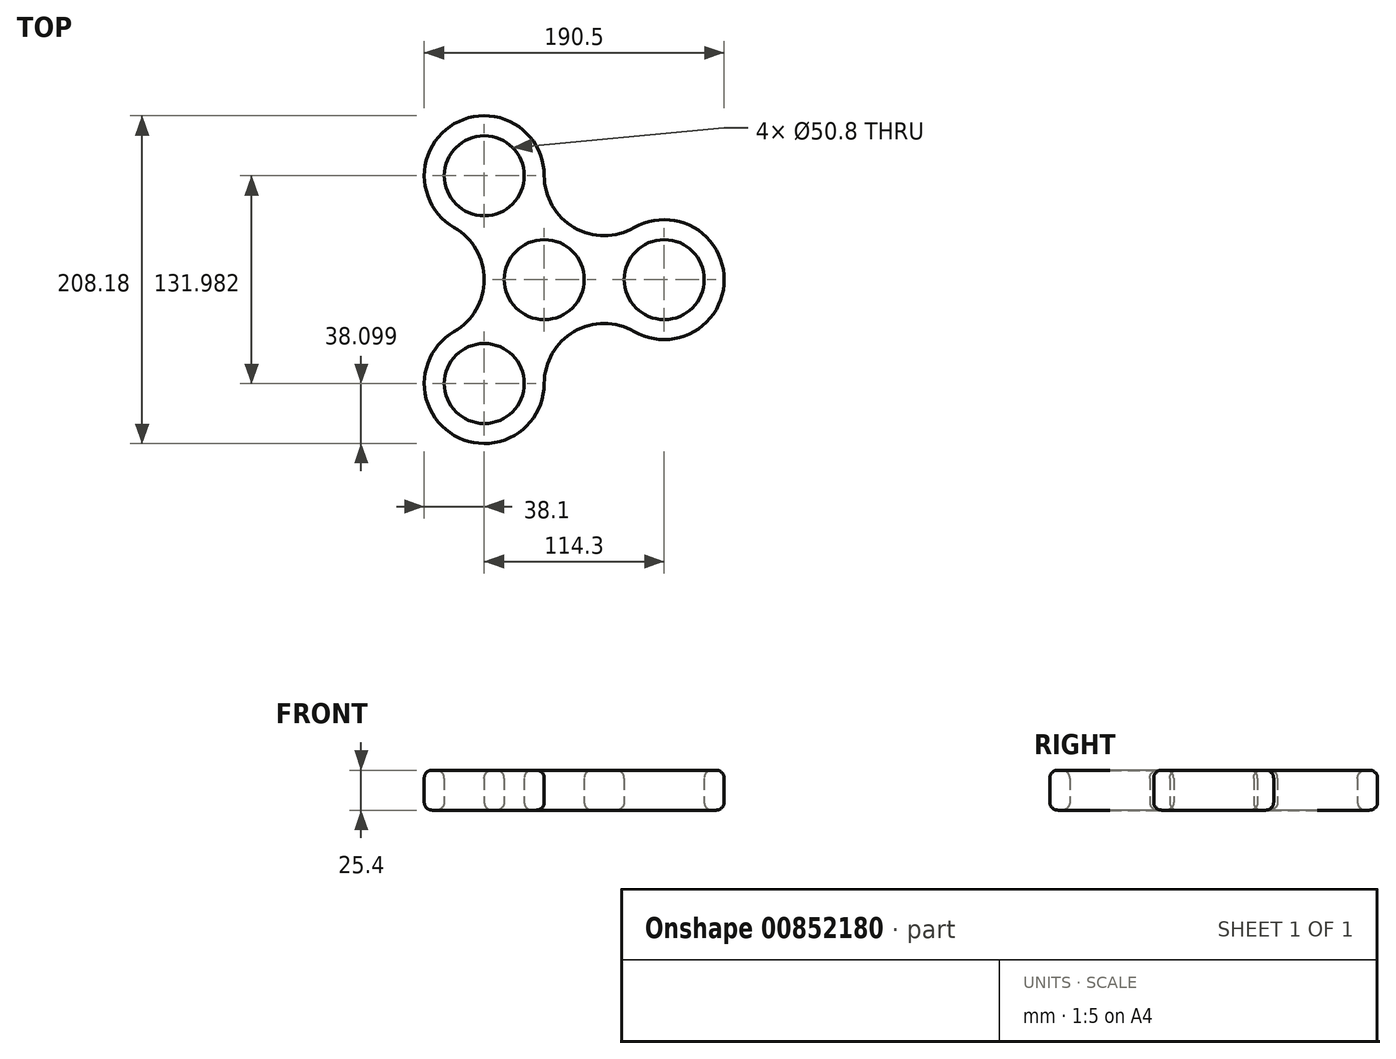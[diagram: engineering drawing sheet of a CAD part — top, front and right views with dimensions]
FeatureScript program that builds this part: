
annotation { "Feature Type Name" : "Feature", "Feature Type Description" : "" }
export const myFeature = defineFeature(function(context is Context, id is Id, definition is map)
    precondition{}
    {
        {
            var Q0;
            Q0=qCreatedBy(makeId("Top.planeOp"),FACE);
            var sketch = newSketch(context, id + "F0", { "sketchPlane" : qUnion([Q0])});
            skCircle(sketch, "E0.cCircle", {"center": v(0, 0) * mm, "radius": 76.2 * mm});
            skLineSegment(sketch, "E0.0", {"start": v(38.1, 66) * mm, "end": v(76.2, 0) * mm});
            skLineSegment(sketch, "E0.1", {"start": v(76.2, 0) * mm, "end": v(38.1, -66) * mm});
            skLineSegment(sketch, "E0.2", {"start": v(38.1, -66) * mm, "end": v(-38.1, -66) * mm});
            skLineSegment(sketch, "E0.3", {"start": v(-38.1, -66) * mm, "end": v(-76.2, 0) * mm});
            skLineSegment(sketch, "E0.4", {"start": v(-76.2, 0) * mm, "end": v(-38.1, 66) * mm});
            skLineSegment(sketch, "E0.5", {"start": v(38.1, 66) * mm, "end": v(76.2, 66) * mm});
            skCircle(sketch, "E1", {"center": v(0, 0) * mm, "radius": 25.4 * mm});
            skCircle(sketch, "E2", {"center": v(-38.1, 66) * mm, "radius": 25.4 * mm});
            skCircle(sketch, "E3", {"center": v(38.1, 66) * mm, "radius": 25.4 * mm});
            skCircle(sketch, "E4", {"center": v(76.2, 0) * mm, "radius": 25.4 * mm});
            skCircle(sketch, "E5", {"center": v(38.1, -66) * mm, "radius": 25.4 * mm});
            skCircle(sketch, "E6", {"center": v(-38.1, -66) * mm, "radius": 25.4 * mm});
            skCircle(sketch, "E7", {"center": v(-76.2, 0) * mm, "radius": 25.4 * mm});
            skCircle(sketch, "E8.0", {"center": v(-38.1, 66) * mm, "radius": 38.1 * mm});
            skCircle(sketch, "E9.0", {"center": v(38.1, 66) * mm, "radius": 38.1 * mm});
            skCircle(sketch, "E10.0", {"center": v(76.2, 0) * mm, "radius": 38.1 * mm});
            skCircle(sketch, "E11.0", {"center": v(-76.2, 0) * mm, "radius": 38.1 * mm});
            skCircle(sketch, "E12.0", {"center": v(-38.1, -66) * mm, "radius": 38.1 * mm});
            skCircle(sketch, "E13.0", {"center": v(38.1, -66) * mm, "radius": 38.1 * mm});
            skSolve(sketch);
        }
        {
            var Q0;
            {var subQ0=sQuery(id+"F0.wireOp",EDGE,"E10.0");var subQ1=sQuery(id+"F0.wireOp",EDGE,"E0.cCircle");var subQ2=makeQuery(id+"F0.imprint","INTERSECT",VERTEX,{"disambiguationData":[OD(0.0)],"derivedFrom":[subQ1,subQ0]});Q0=makeQuery(id+"F0.imprint","IMPRINT",FACE,{"disambiguationData":[TD([[makeQuery(id+"F0.imprint","IMPRINT",EDGE,{"disambiguationData":[TD([[subQ2,1.0]])],"derivedFrom":subQ1}),-1.0]])]});}
            var Q1;
            {var subQ0=sQuery(id+"F0.wireOp",EDGE,"E10.0");var subQ1=sQuery(id+"F0.wireOp",EDGE,"E0.cCircle");var subQ2=makeQuery(id+"F0.imprint","INTERSECT",VERTEX,{"disambiguationData":[OD(0.0)],"derivedFrom":[subQ1,subQ0]});Q1=makeQuery(id+"F0.imprint","IMPRINT",FACE,{"disambiguationData":[TD([[makeQuery(id+"F0.imprint","IMPRINT",EDGE,{"disambiguationData":[TD([[subQ2,1.0]])],"derivedFrom":subQ1}),1.0]])]});}
            var Q2;
            {var subQ0=sQuery(id+"F0.wireOp",EDGE,"E4");var subQ1=sQuery(id+"F0.wireOp",EDGE,"E0.0");var subQ2=makeQuery(id+"F0.imprint","INTERSECT",VERTEX,{"derivedFrom":[subQ1,subQ0]});Q2=makeQuery(id+"F0.imprint","IMPRINT",FACE,{"disambiguationData":[TD([[makeQuery(id+"F0.imprint","IMPRINT",EDGE,{"disambiguationData":[TD([[subQ2,-1.0]])],"derivedFrom":subQ0}),-1.0]])]});}
            var Q3;
            {var subQ0=sQuery(id+"F0.wireOp",EDGE,"E10.0");var subQ1=sQuery(id+"F0.wireOp",EDGE,"E0.cCircle");var subQ2=makeQuery(id+"F0.imprint","INTERSECT",VERTEX,{"disambiguationData":[OD(1.0)],"derivedFrom":[subQ1,subQ0]});Q3=makeQuery(id+"F0.imprint","IMPRINT",FACE,{"disambiguationData":[TD([[makeQuery(id+"F0.imprint","IMPRINT",EDGE,{"disambiguationData":[TD([[subQ2,-1.0]])],"derivedFrom":subQ1}),1.0]])]});}
            var Q4;
            Q4=makeQuery(id+"F0.imprint","IMPRINT",FACE,{"disambiguationData":[TD([[makeQuery(id+"F0.imprint","IMPRINT",EDGE,{"derivedFrom":sQuery(id+"F0.wireOp",EDGE,"E1")}),-1.0]])]});
            var Q5;
            {var subQ0=sQuery(id+"F0.wireOp",EDGE,"E12.0");var subQ1=sQuery(id+"F0.wireOp",EDGE,"E0.cCircle");var subQ2=makeQuery(id+"F0.imprint","INTERSECT",VERTEX,{"disambiguationData":[OD(1.0)],"derivedFrom":[subQ1,subQ0]});Q5=makeQuery(id+"F0.imprint","IMPRINT",FACE,{"disambiguationData":[TD([[makeQuery(id+"F0.imprint","IMPRINT",EDGE,{"disambiguationData":[TD([[subQ2,1.0]])],"derivedFrom":subQ1}),1.0]])]});}
            var Q6;
            {var subQ0=sQuery(id+"F0.wireOp",EDGE,"E6");var subQ1=sQuery(id+"F0.wireOp",EDGE,"E0.2");var subQ2=makeQuery(id+"F0.imprint","INTERSECT",VERTEX,{"derivedFrom":[subQ1,subQ0]});Q6=makeQuery(id+"F0.imprint","IMPRINT",FACE,{"disambiguationData":[TD([[makeQuery(id+"F0.imprint","IMPRINT",EDGE,{"disambiguationData":[TD([[subQ2,-1.0]])],"derivedFrom":subQ0}),-1.0]])]});}
            var Q7;
            {var subQ0=sQuery(id+"F0.wireOp",EDGE,"E12.0");var subQ1=sQuery(id+"F0.wireOp",EDGE,"E0.cCircle");var subQ2=makeQuery(id+"F0.imprint","INTERSECT",VERTEX,{"disambiguationData":[OD(0.0)],"derivedFrom":[subQ1,subQ0]});Q7=makeQuery(id+"F0.imprint","IMPRINT",FACE,{"disambiguationData":[TD([[makeQuery(id+"F0.imprint","IMPRINT",EDGE,{"disambiguationData":[TD([[subQ2,-1.0]])],"derivedFrom":subQ1}),-1.0]])]});}
            var Q8;
            {var subQ0=sQuery(id+"F0.wireOp",EDGE,"E12.0");var subQ1=sQuery(id+"F0.wireOp",EDGE,"E0.cCircle");var subQ2=makeQuery(id+"F0.imprint","INTERSECT",VERTEX,{"disambiguationData":[OD(0.0)],"derivedFrom":[subQ1,subQ0]});Q8=makeQuery(id+"F0.imprint","IMPRINT",FACE,{"disambiguationData":[TD([[makeQuery(id+"F0.imprint","IMPRINT",EDGE,{"disambiguationData":[TD([[subQ2,-1.0]])],"derivedFrom":subQ1}),1.0]])]});}
            var Q9;
            {var subQ0=sQuery(id+"F0.wireOp",EDGE,"E8.0");var subQ1=sQuery(id+"F0.wireOp",EDGE,"E0.cCircle");var subQ2=makeQuery(id+"F0.imprint","INTERSECT",VERTEX,{"disambiguationData":[OD(1.0)],"derivedFrom":[subQ1,subQ0]});Q9=makeQuery(id+"F0.imprint","IMPRINT",FACE,{"disambiguationData":[TD([[makeQuery(id+"F0.imprint","IMPRINT",EDGE,{"disambiguationData":[TD([[subQ2,1.0]])],"derivedFrom":subQ1}),1.0]])]});}
            var Q10;
            {var subQ0=sQuery(id+"F0.wireOp",EDGE,"E8.0");var subQ1=sQuery(id+"F0.wireOp",EDGE,"E0.cCircle");var subQ2=makeQuery(id+"F0.imprint","INTERSECT",VERTEX,{"disambiguationData":[OD(0.0)],"derivedFrom":[subQ1,subQ0]});Q10=makeQuery(id+"F0.imprint","IMPRINT",FACE,{"disambiguationData":[TD([[makeQuery(id+"F0.imprint","IMPRINT",EDGE,{"disambiguationData":[TD([[subQ2,-1.0]])],"derivedFrom":subQ1}),1.0]])]});}
            var Q11;
            {var subQ0=sQuery(id+"F0.wireOp",EDGE,"E8.0");var subQ1=sQuery(id+"F0.wireOp",EDGE,"E0.cCircle");var subQ2=makeQuery(id+"F0.imprint","INTERSECT",VERTEX,{"disambiguationData":[OD(0.0)],"derivedFrom":[subQ1,subQ0]});Q11=makeQuery(id+"F0.imprint","IMPRINT",FACE,{"disambiguationData":[TD([[makeQuery(id+"F0.imprint","IMPRINT",EDGE,{"disambiguationData":[TD([[subQ2,-1.0]])],"derivedFrom":subQ1}),-1.0]])]});}
            extrude(context, id + "F1", {"entities" : qUnion([Q0, Q1, Q2, Q3, Q4, Q5, Q6, Q7, Q8, Q9, Q10, Q11]), "depth" : 25.4 * mm, "offsetDistance" : 25.4 * mm});
        }
        {
            var Q0;
            Q0=makeQuery(id+"F1.opExtrude","CAP_EDGE",EDGE,{"disambiguationData":[OSD([sQuery(id+"F0.wireOp",EDGE,"E9.0")])],"isStart":false});
            var Q1;
            Q1=makeQuery(id+"F1.opExtrude","CAP_FACE",FACE,{"disambiguationData":[OSD([sQuery(id+"F0.wireOp",EDGE,"E1"),sQuery(id+"F0.wireOp",EDGE,"E2"),sQuery(id+"F0.wireOp",EDGE,"E4"),sQuery(id+"F0.wireOp",EDGE,"E6"),sQuery(id+"F0.wireOp",EDGE,"E8.0"),sQuery(id+"F0.wireOp",EDGE,"E9.0"),sQuery(id+"F0.wireOp",EDGE,"E10.0"),sQuery(id+"F0.wireOp",EDGE,"E11.0"),sQuery(id+"F0.wireOp",EDGE,"E12.0"),sQuery(id+"F0.wireOp",EDGE,"E13.0")])],"isStart":false});
            fillet(context, id + "F2", {"entities" : qUnion([Q0, Q1]), "radius" : 5.08 * mm, "tangentPropagation" : true, "allowEdgeOverflow" : false});
        }
        {
            var Q0;
            Q0=makeQuery(id+"F1.opExtrude","CAP_FACE",FACE,{"disambiguationData":[OSD([sQuery(id+"F0.wireOp",EDGE,"E1"),sQuery(id+"F0.wireOp",EDGE,"E2"),sQuery(id+"F0.wireOp",EDGE,"E4"),sQuery(id+"F0.wireOp",EDGE,"E6"),sQuery(id+"F0.wireOp",EDGE,"E8.0"),sQuery(id+"F0.wireOp",EDGE,"E9.0"),sQuery(id+"F0.wireOp",EDGE,"E10.0"),sQuery(id+"F0.wireOp",EDGE,"E11.0"),sQuery(id+"F0.wireOp",EDGE,"E12.0"),sQuery(id+"F0.wireOp",EDGE,"E13.0")])],"isStart":true});
            fillet(context, id + "F3", {"entities" : qUnion([Q0]), "radius" : 5.08 * mm, "tangentPropagation" : true, "allowEdgeOverflow" : false});
        }
    });
